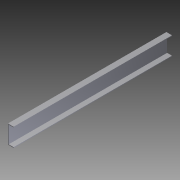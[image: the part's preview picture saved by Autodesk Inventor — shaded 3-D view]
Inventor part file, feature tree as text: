
AUTODESK INVENTOR PART (.ipt)
format: ipt  version: 2012 (Build 160160000, 160)  size: 77,824 bytes
history: native  units: in
note: dims shown in document units (in); Inventor stores cm internally (conversion verified against a paired STEP export)
features: extrude x1, sketch x1
ambient origin geometry x8: Origin, YZ Plane, XZ Plane, XY Plane, X Axis, Y Axis, Z Axis, Center Point
bodies: Solid1 (feature_tree)
feature tree (2):
  extrude  "Extrusion1"  Depth=1.0in
  sketch  "Sketch1"  dims[d0=3.25in d1=1.0in d2=0.125in d3=0.125in d4=28.0in d5=0.0in d6=0.125in d7=1.0in]
